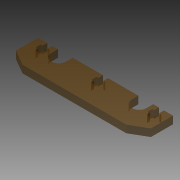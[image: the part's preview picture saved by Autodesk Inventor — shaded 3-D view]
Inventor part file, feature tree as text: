
AUTODESK INVENTOR PART (.ipt)
format: ipt  version: 2014 SP1 (Build 180222100, 222)  size: 151,040 bytes
history: native  units: mm
features: extrude x1, sketch x1
ambient origin geometry x8: Origin, YZ Plane, XZ Plane, XY Plane, X Axis, Y Axis, Z Axis, Center Point
bodies: Solid1 (feature_tree)
feature tree (2):
  extrude  "Extrusion1"  [1 undecoded]
  sketch  "Sketch1"  dims[d0=4.7625mm d1=0.0mm]
note: 1 required parameter value undecoded (feature->parameter linkage not recoverable at this tier; creation-order binding heuristic only, values carry confidence <= 0.55)
